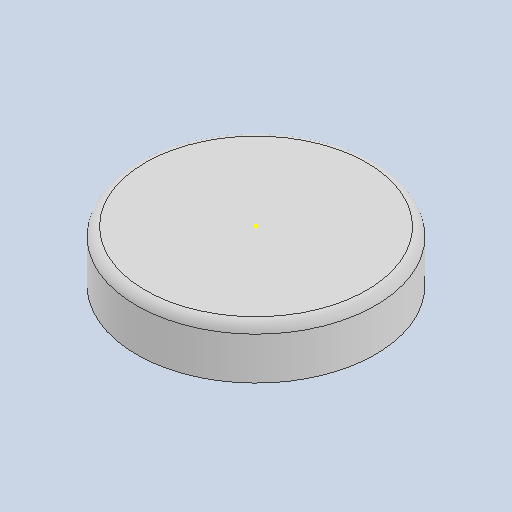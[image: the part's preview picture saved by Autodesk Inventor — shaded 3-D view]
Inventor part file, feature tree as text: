
AUTODESK INVENTOR PART (.ipt)
format: ipt  version: 2023 (Build 270158000, 158)  size: 263,680 bytes
history: native  units: in
note: dims shown in document units (in); Inventor stores cm internally (conversion verified against a paired STEP export)
features: sketch x5, extrude x4, fillet x1
ambient origin geometry x8: Origin, YZ Plane, XZ Plane, XY Plane, X Axis, Y Axis, Z Axis, Center Point
bodies: Solid1 (feature_tree)
feature tree (10):
  extrude  "Extrusion1"  Depth=1.1811in TaperAngle=0.0deg
  sketch  "Sketch2"  dims[d4=5.1181in d5=0.9843in d6=0.0in]
  fillet  "Fillet1"  Radius=0.2037in
  extrude  "Extrusion2"  Depth=0.9843in TaperAngle=0.0deg
  extrude  "Extrusion4"  Depth=0.2362in
  extrude  "Extrusion5"  Depth=0.1969in
  sketch  "Sketch1"  dims[d0=5.5118in d1=1.1811in d2=0.0in d3=0.2037in]
  sketch  "Sketch3"  dims[d11=0.2756in d12=0.2362in]
  sketch  "Sketch5"  dims[d13=0.7874in d14=0.0in d15=0.1969in]
  sketch  "Sketch6"  dims[d16=0.1181in d17=0.7874in d18=0.0in d19=0.0197in d20=0.0344in d21=0.0197in d22=0.0344in]
